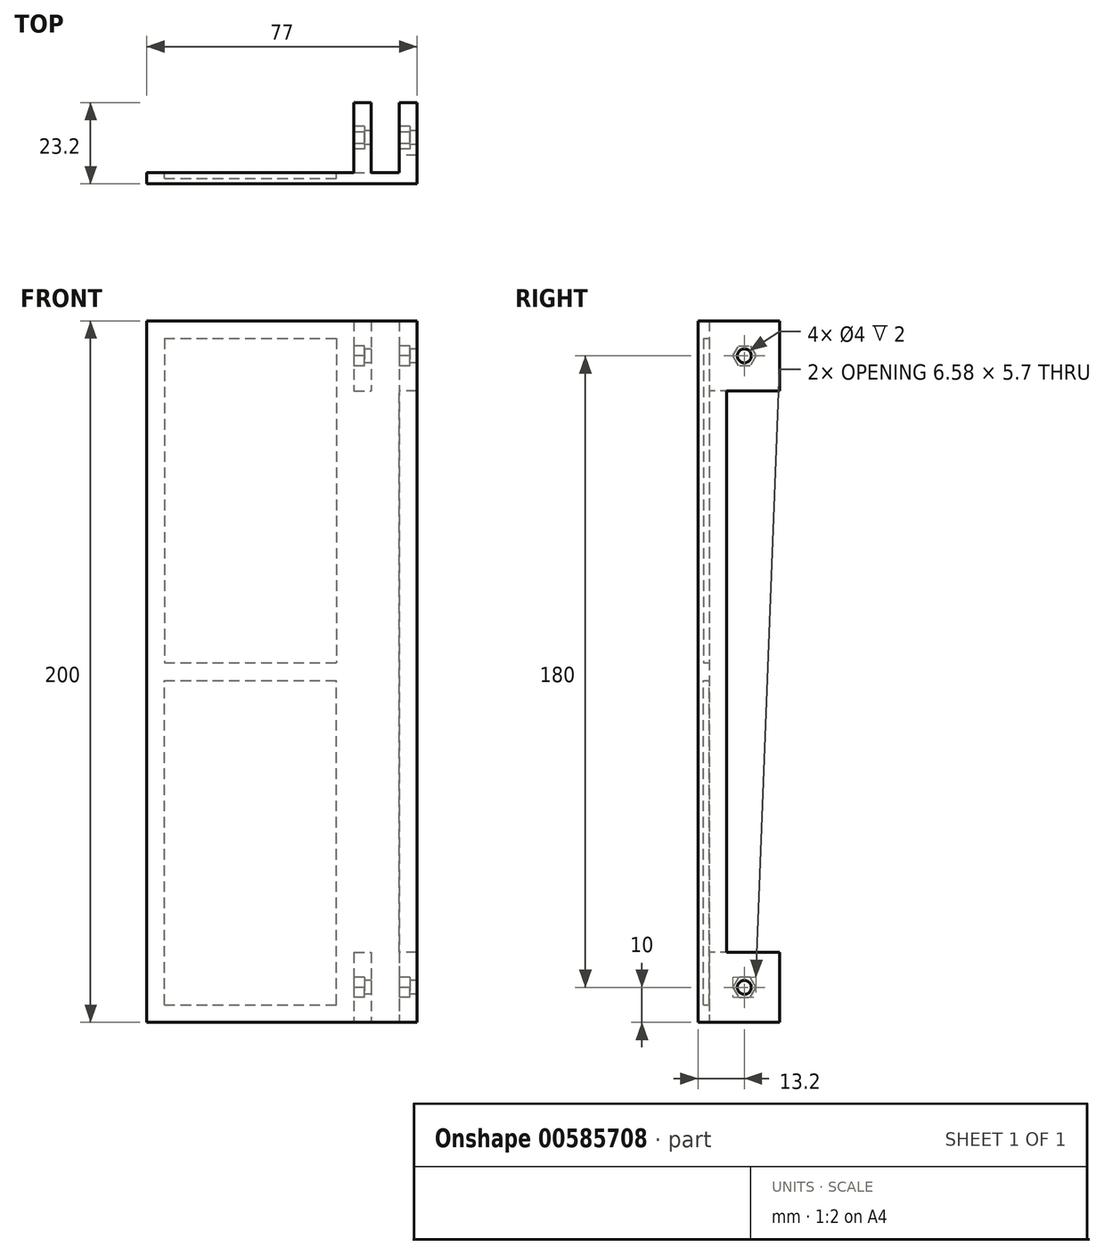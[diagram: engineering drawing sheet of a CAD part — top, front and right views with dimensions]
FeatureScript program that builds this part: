
annotation { "Feature Type Name" : "Feature", "Feature Type Description" : "" }
export const myFeature = defineFeature(function(context is Context, id is Id, definition is map)
    precondition{}
    {
        {
            var Q0;
            Q0=qCreatedBy(makeId("Front.planeOp"),FACE);
            var sketch = newSketch(context, id + "F0", { "sketchPlane" : qUnion([Q0])});
            skLineSegment(sketch, "E0.bottom", {"start": v(0, 0) * mm, "end": v(60, 0) * mm});
            skLineSegment(sketch, "E0.top", {"start": v(0, 200) * mm, "end": v(60, 200) * mm});
            skLineSegment(sketch, "E0.left", {"start": v(0, 0) * mm, "end": v(0, 200) * mm});
            skLineSegment(sketch, "E0.right", {"start": v(60, 0) * mm, "end": v(60, 200) * mm});
            skSolve(sketch);
        }
        {
            var Q0;
            Q0 = qSketchRegion(id + "F0", true);
            extrude(context, id + "F1", {"entities" : qUnion([Q0]), "depth" : 3.2 * mm, "offsetDistance" : 25 * mm});
        }
        {
            var Q0;
            Q0=makeQuery(id+"F1.opExtrude","CAP_FACE",FACE,{"disambiguationData":[OSD([sQuery(id+"F0.wireOp",EDGE,"E0.bottom"),sQuery(id+"F0.wireOp",EDGE,"E0.top"),sQuery(id+"F0.wireOp",EDGE,"E0.left"),sQuery(id+"F0.wireOp",EDGE,"E0.right")])],"isStart":true});
            var sketch = newSketch(context, id + "F2", { "sketchPlane" : qUnion([Q0])});
            skLineSegment(sketch, "E1.bottom", {"start": v(-60, 200) * mm, "end": v(-57, 200) * mm});
            skLineSegment(sketch, "E1.top", {"start": v(-60, 0) * mm, "end": v(-57, 0) * mm});
            skLineSegment(sketch, "E1.left", {"start": v(-60, 200) * mm, "end": v(-60, 180) * mm});
            skLineSegment(sketch, "E1.right", {"start": v(-57, 200) * mm, "end": v(-57, 180) * mm});
            skLineSegment(sketch, "E2.bottom", {"start": v(-49, 200) * mm, "end": v(-46, 200) * mm});
            skLineSegment(sketch, "E2.top", {"start": v(-49, 0) * mm, "end": v(-46, 0) * mm});
            skLineSegment(sketch, "E2.left", {"start": v(-49, 200) * mm, "end": v(-49, 180) * mm});
            skLineSegment(sketch, "E2.right", {"start": v(-46, 200) * mm, "end": v(-46, 180) * mm});
            skLineSegment(sketch, "E3", {"start": v(-46, 180) * mm, "end": v(-49, 180) * mm});
            skLineSegment(sketch, "E4", {"start": v(-60, 100) * mm, "end": v(-21.47, 100) * mm, "construction": true});
            skLineSegment(sketch, "E5.MirrorCS", {"start": v(-46, 20) * mm, "end": v(-49, 20) * mm});
            skLineSegment(sketch, "E6.trimOffspring", {"start": v(-46, 20) * mm, "end": v(-46, 0) * mm});
            skLineSegment(sketch, "E7.trimOffspring", {"start": v(-49, 20) * mm, "end": v(-49, 0) * mm});
            skLineSegment(sketch, "E8.trimOffspring", {"start": v(-57, 20) * mm, "end": v(-57, 0) * mm});
            skLineSegment(sketch, "E9.trimOffspring", {"start": v(-60, 20) * mm, "end": v(-60, 0) * mm});
            skLineSegment(sketch, "E10.trimOffspring", {"start": v(-57, 180) * mm, "end": v(-60, 180) * mm});
            skLineSegment(sketch, "E11.trimOffspring", {"start": v(-57, 20) * mm, "end": v(-60, 20) * mm});
            skSolve(sketch);
        }
        {
            var Q0;
            Q0 = qSketchRegion(id + "F2", true);
            extrude(context, id + "F3", {"entities" : qUnion([Q0]), "operationType" : NewBodyOperationType.ADD, "depth" : 20 * mm, "offsetDistance" : 25 * mm});
        }
        {
            var Q0;
            Q0=makeQuery(id+"F1.opExtrude","CAP_FACE",FACE,{"disambiguationData":[OSD([sQuery(id+"F0.wireOp",EDGE,"E0.bottom"),sQuery(id+"F0.wireOp",EDGE,"E0.top"),sQuery(id+"F0.wireOp",EDGE,"E0.left"),sQuery(id+"F0.wireOp",EDGE,"E0.right")])],"isStart":false});
            var sketch = newSketch(context, id + "F4", { "sketchPlane" : qUnion([Q0])});
            skCircle(sketch, "E12", {"center": v(33, 120) * mm, "radius": 7.5 * mm});
            skSolve(sketch);
        }
        {
            var Q0;
            Q0=makeQuery(id+"F1.opExtrude","SWEPT_FACE",FACE,{"disambiguationData":[OSD([sQuery(id+"F0.wireOp",EDGE,"E0.left")])]});
            extrude(context, id + "F5", {"entities" : qUnion([Q0]), "operationType" : NewBodyOperationType.ADD, "depth" : 15 * mm, "offsetDistance" : 25 * mm});
        }
        {
            var Q0;
            Q0=makeQuery(id+"F3.boolean.opBoolean","MERGE",FACE,{"derivedFrom":[makeQuery(id+"F1.opExtrude","SWEPT_FACE",FACE,{"disambiguationData":[OSD([sQuery(id+"F0.wireOp",EDGE,"E0.right")])]}),makeQuery(id+"F3.opExtrude","SWEPT_FACE",FACE,{"disambiguationData":[OSD([sQuery(id+"F2.wireOp",EDGE,"E1.left")])]}),makeQuery(id+"F3.opExtrude","SWEPT_FACE",FACE,{"disambiguationData":[OSD([sQuery(id+"F2.wireOp",EDGE,"E9.trimOffspring")])]})]});
            extrude(context, id + "F6", {"entities" : qUnion([Q0]), "operationType" : NewBodyOperationType.ADD, "depth" : 2 * mm, "offsetDistance" : 25 * mm});
        }
        {
            var Q0;
            Q0=makeQuery(id+"F3.opExtrude","SWEPT_FACE",FACE,{"disambiguationData":[OSD([sQuery(id+"F2.wireOp",EDGE,"E2.right")])]});
            var Q1;
            Q1=makeQuery(id+"F3.opExtrude","SWEPT_FACE",FACE,{"disambiguationData":[OSD([sQuery(id+"F2.wireOp",EDGE,"E6.trimOffspring")])]});
            extrude(context, id + "F7", {"entities" : qUnion([Q0, Q1]), "operationType" : NewBodyOperationType.ADD, "depth" : 2 * mm, "offsetDistance" : 25 * mm});
        }
        {
            var Q0;
            Q0=makeQuery(id+"F3.opExtrude","SWEPT_FACE",FACE,{"disambiguationData":[OSD([sQuery(id+"F2.wireOp",EDGE,"E8.trimOffspring")])]});
            var sketch = newSketch(context, id + "F8", { "sketchPlane" : qUnion([Q0])});
            skLineSegment(sketch, "E13", {"start": v(-27.16, 100) * mm, "end": v(3.2, 100) * mm, "construction": true});
            skCircle(sketch, "E14", {"center": v(-10, 10) * mm, "radius": 2 * mm});
            skCircle(sketch, "E15.cCircle", {"center": v(-10, 10) * mm, "radius": 2.85 * mm, "construction": true});
            skLineSegment(sketch, "E15.0", {"start": v(-8.35, 12.85) * mm, "end": v(-6.7, 10) * mm});
            skLineSegment(sketch, "E15.1", {"start": v(-6.7, 10) * mm, "end": v(-8.35, 7.15) * mm});
            skLineSegment(sketch, "E15.2", {"start": v(-8.35, 7.15) * mm, "end": v(-11.65, 7.15) * mm});
            skLineSegment(sketch, "E15.3", {"start": v(-11.65, 7.15) * mm, "end": v(-13.3, 10) * mm});
            skLineSegment(sketch, "E15.4", {"start": v(-13.3, 10) * mm, "end": v(-11.65, 12.85) * mm});
            skLineSegment(sketch, "E15.5", {"start": v(-11.65, 12.85) * mm, "end": v(-8.35, 12.85) * mm});
            skPoint(sketch, "E15.0.midPoint", {"position": v(-7.53, 11.43) * mm});
            skLineSegment(sketch, "E16", {"start": v(3, 10) * mm, "end": v(-20, 10) * mm, "construction": true});
            skLineSegment(sketch, "E17", {"start": v(-10, 20) * mm, "end": v(-10, 16.33) * mm, "construction": true});
            skLineSegment(sketch, "E18.MirrorCS", {"start": v(-8.35, 187.15) * mm, "end": v(-6.7, 190) * mm});
            skLineSegment(sketch, "E19.MirrorCS", {"start": v(-11.65, 187.15) * mm, "end": v(-8.35, 187.15) * mm});
            skCircle(sketch, "E20.MirrorC", {"center": v(-10, 190) * mm, "radius": 2 * mm});
            skCircle(sketch, "E21.MirrorC", {"center": v(-10, 190) * mm, "radius": 2.85 * mm, "construction": true});
            skLineSegment(sketch, "E22.MirrorCS", {"start": v(-6.7, 190) * mm, "end": v(-8.35, 192.85) * mm});
            skLineSegment(sketch, "E23.MirrorCS", {"start": v(-8.35, 192.85) * mm, "end": v(-11.65, 192.85) * mm});
            skLineSegment(sketch, "E24.MirrorCS", {"start": v(-11.65, 192.85) * mm, "end": v(-13.3, 190) * mm});
            skLineSegment(sketch, "E25.MirrorCS", {"start": v(-13.3, 190) * mm, "end": v(-11.65, 187.15) * mm});
            skLineSegment(sketch, "E26.MirrorCS", {"start": v(3, 190) * mm, "end": v(-20, 190) * mm, "construction": true});
            skLineSegment(sketch, "E27.MirrorCS", {"start": v(-10, 180) * mm, "end": v(-10, 183.67) * mm, "construction": true});
            skPoint(sketch, "E28.MirrorP", {"position": v(-7.53, 188.57) * mm});
            skPoint(sketch, "E29.0", {"position": v(-20, 10) * mm});
            skPoint(sketch, "E30.0", {"position": v(3.2, 100) * mm});
            skSolve(sketch);
        }
        {
            var Q0;
            Q0 = qSketchRegion(id + "F8", true);
            extrude(context, id + "F9", {"entities" : qUnion([Q0]), "operationType" : NewBodyOperationType.REMOVE, "oppositeDirection" : true, "depth" : 3 * mm, "offsetDistance" : 25 * mm});
        }
        {
            var Q0;
            Q0=makeQuery(id+"F9.boolean.opBoolean","SPLIT",FACE,{"disambiguationData":[TD([makeQuery(id+"F9.opExtrude","SWEPT_FACE",FACE,{"disambiguationData":[OSD([sQuery(id+"F8.wireOp",EDGE,"E14")])]})])],"derivedFrom":makeQuery(id+"F3.opExtrude","SWEPT_FACE",FACE,{"disambiguationData":[OSD([sQuery(id+"F2.wireOp",EDGE,"E8.trimOffspring")])]})});
            var Q1;
            Q1=makeQuery(id+"F9.boolean.opBoolean","SPLIT",FACE,{"disambiguationData":[TD([makeQuery(id+"F9.opExtrude","SWEPT_FACE",FACE,{"disambiguationData":[OSD([sQuery(id+"F8.wireOp",EDGE,"E20.MirrorC")])]})])],"derivedFrom":makeQuery(id+"F3.opExtrude","SWEPT_FACE",FACE,{"disambiguationData":[OSD([sQuery(id+"F2.wireOp",EDGE,"E1.right")])]})});
            extrude(context, id + "F10", {"entities" : qUnion([Q0, Q1]), "operationType" : NewBodyOperationType.REMOVE, "oppositeDirection" : true, "depth" : 25 * mm, "offsetDistance" : 25 * mm});
        }
        {
            var Q0;
            Q0=makeQuery(id+"F7.opExtrude","CAP_FACE",FACE,{"disambiguationData":[OSD([sQuery(id+"F2.wireOp",EDGE,"E6.trimOffspring")])],"isStart":false});
            var sketch = newSketch(context, id + "F11", { "sketchPlane" : qUnion([Q0])});
            skLineSegment(sketch, "E31", {"start": v(-25.76, 100) * mm, "end": v(3.2, 100) * mm, "construction": true});
            skCircle(sketch, "E32", {"center": v(-10, 10) * mm, "radius": 2 * mm});
            skCircle(sketch, "E33.cCircle", {"center": v(-10, 10) * mm, "radius": 2.85 * mm, "construction": true});
            skLineSegment(sketch, "E33.0", {"start": v(-8.35, 12.85) * mm, "end": v(-6.7, 10) * mm});
            skLineSegment(sketch, "E33.1", {"start": v(-6.7, 10) * mm, "end": v(-8.35, 7.15) * mm});
            skLineSegment(sketch, "E33.2", {"start": v(-8.35, 7.15) * mm, "end": v(-11.65, 7.15) * mm});
            skLineSegment(sketch, "E33.3", {"start": v(-11.65, 7.15) * mm, "end": v(-13.3, 10) * mm});
            skLineSegment(sketch, "E33.4", {"start": v(-13.3, 10) * mm, "end": v(-11.65, 12.85) * mm});
            skLineSegment(sketch, "E33.5", {"start": v(-11.65, 12.85) * mm, "end": v(-8.35, 12.85) * mm});
            skPoint(sketch, "E33.0.midPoint", {"position": v(-7.53, 11.43) * mm});
            skLineSegment(sketch, "E34", {"start": v(3, 10) * mm, "end": v(-20, 10) * mm, "construction": true});
            skLineSegment(sketch, "E35", {"start": v(-10, 20) * mm, "end": v(-10, 6.7) * mm, "construction": true});
            skLineSegment(sketch, "E36.MirrorCS", {"start": v(-8.35, 187.15) * mm, "end": v(-6.7, 190) * mm});
            skLineSegment(sketch, "E37.MirrorCS", {"start": v(-11.65, 187.15) * mm, "end": v(-8.35, 187.15) * mm});
            skCircle(sketch, "E38.MirrorC", {"center": v(-10, 190) * mm, "radius": 2 * mm});
            skCircle(sketch, "E39.MirrorC", {"center": v(-10, 190) * mm, "radius": 2.85 * mm, "construction": true});
            skLineSegment(sketch, "E40.MirrorCS", {"start": v(-6.7, 190) * mm, "end": v(-8.35, 192.85) * mm});
            skLineSegment(sketch, "E41.MirrorCS", {"start": v(-8.35, 192.85) * mm, "end": v(-11.65, 192.85) * mm});
            skLineSegment(sketch, "E42.MirrorCS", {"start": v(-11.65, 192.85) * mm, "end": v(-13.3, 190) * mm});
            skLineSegment(sketch, "E43.MirrorCS", {"start": v(-13.3, 190) * mm, "end": v(-11.65, 187.15) * mm});
            skLineSegment(sketch, "E44.MirrorCS", {"start": v(3, 190) * mm, "end": v(-20, 190) * mm, "construction": true});
            skLineSegment(sketch, "E45.MirrorCS", {"start": v(-10, 180) * mm, "end": v(-10, 193.3) * mm, "construction": true});
            skPoint(sketch, "E46.MirrorP", {"position": v(-7.53, 188.58) * mm});
            skSolve(sketch);
        }
        {
            var Q0;
            Q0 = qSketchRegion(id + "F11", true);
            extrude(context, id + "F12", {"entities" : qUnion([Q0]), "operationType" : NewBodyOperationType.REMOVE, "oppositeDirection" : true, "depth" : 3 * mm, "offsetDistance" : 25 * mm});
        }
        {
            var Q0;
            Q0=makeQuery(id+"F12.boolean.opBoolean","SPLIT",FACE,{"disambiguationData":[TD([makeQuery(id+"F12.opExtrude","SWEPT_FACE",FACE,{"disambiguationData":[OSD([sQuery(id+"F11.wireOp",EDGE,"E38.MirrorC")])]})])],"derivedFrom":makeQuery(id+"F7.opExtrude","CAP_FACE",FACE,{"disambiguationData":[OSD([sQuery(id+"F2.wireOp",EDGE,"E2.right")])],"isStart":false})});
            var Q1;
            Q1=makeQuery(id+"F12.boolean.opBoolean","SPLIT",FACE,{"disambiguationData":[TD([makeQuery(id+"F12.opExtrude","SWEPT_FACE",FACE,{"disambiguationData":[OSD([sQuery(id+"F11.wireOp",EDGE,"E32")])]})])],"derivedFrom":makeQuery(id+"F7.opExtrude","CAP_FACE",FACE,{"disambiguationData":[OSD([sQuery(id+"F2.wireOp",EDGE,"E6.trimOffspring")])],"isStart":false})});
            extrude(context, id + "F13", {"entities" : qUnion([Q0, Q1]), "operationType" : NewBodyOperationType.REMOVE, "oppositeDirection" : true, "depth" : 25 * mm, "offsetDistance" : 25 * mm});
        }
        {
            var Q0;
            {var subQ0=sQuery(id+"F2.wireOp",EDGE,"E10.trimOffspring");Q0=makeQuery(id+"F6.boolean.opBoolean","MERGE",FACE,{"derivedFrom":[makeQuery(id+"F3.opExtrude","SWEPT_FACE",FACE,{"disambiguationData":[OSD([subQ0])]}),makeQuery(id+"F6.opExtrude","SWEPT_FACE",FACE,{"disambiguationData":[OSD([sQuery(id+"F0.wireOp",EDGE,"E0.right"),sQuery(id+"F2.wireOp",EDGE,"E1.left"),subQ0])]})]});}
            var sketch = newSketch(context, id + "F14", { "sketchPlane" : qUnion([Q0])});
            skLineSegment(sketch, "E47.bottom", {"start": v(62, 0) * mm, "end": v(57, 0) * mm});
            skLineSegment(sketch, "E47.top", {"start": v(62, -5) * mm, "end": v(57, -5) * mm});
            skLineSegment(sketch, "E47.left", {"start": v(62, 0) * mm, "end": v(62, -5) * mm});
            skLineSegment(sketch, "E47.right", {"start": v(57, 0) * mm, "end": v(57, -5) * mm});
            skSolve(sketch);
        }
        {
            var Q0;
            Q0 = qSketchRegion(id + "F14", true);
            var Q1;
            {var subQ0=sQuery(id+"F2.wireOp",EDGE,"E11.trimOffspring");Q1=makeQuery(id+"F6.boolean.opBoolean","MERGE",FACE,{"derivedFrom":[makeQuery(id+"F3.opExtrude","SWEPT_FACE",FACE,{"disambiguationData":[OSD([subQ0])]}),makeQuery(id+"F6.opExtrude","SWEPT_FACE",FACE,{"disambiguationData":[OSD([sQuery(id+"F0.wireOp",EDGE,"E0.right"),sQuery(id+"F2.wireOp",EDGE,"E9.trimOffspring"),subQ0])]})]});}
            extrude(context, id + "F15", {"entities" : qUnion([Q0]), "operationType" : NewBodyOperationType.ADD, "endBound" : BoundingType.UP_TO_SURFACE, "depth" : 25 * mm, "endBoundEntityFace" : qUnion([Q1]), "offsetDistance" : 25 * mm});
        }
        {
            var Q0;
            {var subQ0=sQuery(id+"F0.wireOp",EDGE,"E0.right");var subQ1=sQuery(id+"F0.wireOp",EDGE,"E0.left");Q0=makeQuery(id+"F6.boolean.opBoolean","MERGE",FACE,{"derivedFrom":[makeQuery(id+"F5.boolean.opBoolean","MERGE",FACE,{"derivedFrom":[makeQuery(id+"F1.opExtrude","CAP_FACE",FACE,{"disambiguationData":[OSD([sQuery(id+"F0.wireOp",EDGE,"E0.bottom"),sQuery(id+"F0.wireOp",EDGE,"E0.top"),subQ1,subQ0])],"isStart":true}),makeQuery(id+"F5.opExtrude","SWEPT_FACE",FACE,{"disambiguationData":[OSD([subQ1]),TDD([makeQuery(id+"F1.opExtrude","CAP_EDGE",EDGE,{"disambiguationData":[OSD([subQ1])],"isStart":true})])]})]}),makeQuery(id+"F6.opExtrude","SWEPT_FACE",FACE,{"disambiguationData":[OSD([subQ0]),TDD([makeQuery(id+"F1.opExtrude","CAP_EDGE",EDGE,{"disambiguationData":[OSD([subQ0])],"isStart":true})])]})]});}
            var sketch = newSketch(context, id + "F16", { "sketchPlane" : qUnion([Q0])});
            skLineSegment(sketch, "E48", {"start": v(15, 100) * mm, "end": v(-90.33, 100) * mm, "construction": true});
            skPoint(sketch, "E48.endSnap0", {"position": v(15, 100) * mm});
            skLineSegment(sketch, "E49.bottom", {"start": v(10, 5) * mm, "end": v(-39, 5) * mm});
            skLineSegment(sketch, "E49.top", {"start": v(10, 97.5) * mm, "end": v(-39, 97.5) * mm});
            skLineSegment(sketch, "E49.left", {"start": v(10, 5) * mm, "end": v(10, 97.5) * mm});
            skLineSegment(sketch, "E49.right", {"start": v(-39, 5) * mm, "end": v(-39, 97.5) * mm});
            skLineSegment(sketch, "E50.MirrorCS", {"start": v(-39, 195) * mm, "end": v(-39, 102.5) * mm});
            skLineSegment(sketch, "E51.MirrorCS", {"start": v(10, 195) * mm, "end": v(10, 102.5) * mm});
            skLineSegment(sketch, "E52.MirrorCS", {"start": v(10, 102.5) * mm, "end": v(-39, 102.5) * mm});
            skLineSegment(sketch, "E53.MirrorCS", {"start": v(10, 195) * mm, "end": v(-39, 195) * mm});
            skSolve(sketch);
        }
        {
            var Q0;
            Q0 = qSketchRegion(id + "F16", true);
            extrude(context, id + "F17", {"entities" : qUnion([Q0]), "operationType" : NewBodyOperationType.REMOVE, "oppositeDirection" : true, "depth" : 1.6 * mm, "offsetDistance" : 25 * mm});
        }
    });
